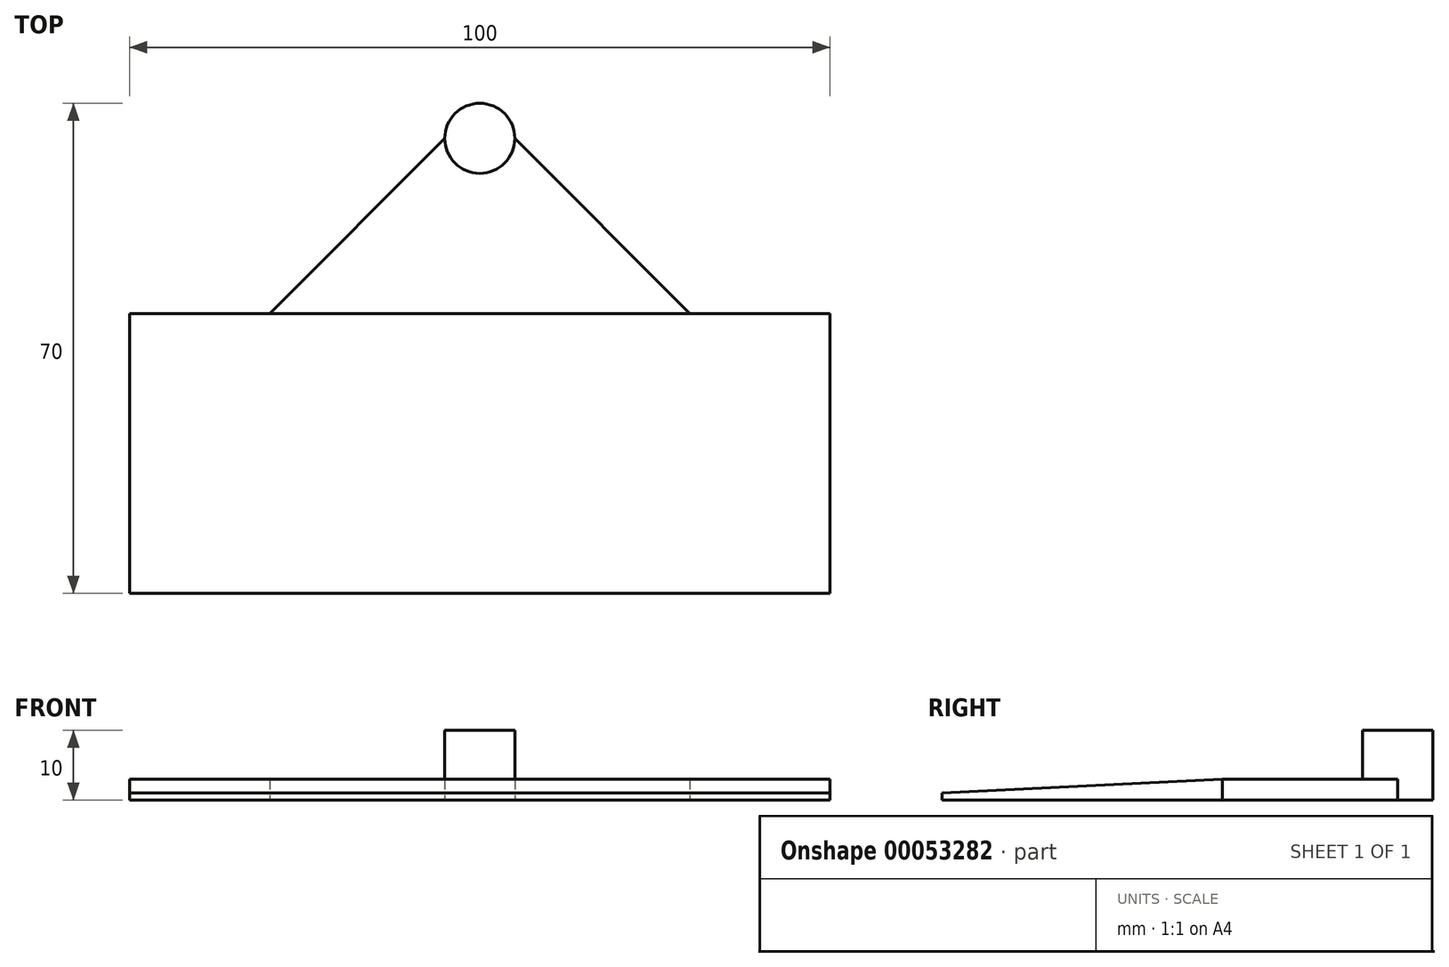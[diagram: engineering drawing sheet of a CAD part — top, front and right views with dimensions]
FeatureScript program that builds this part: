
annotation { "Feature Type Name" : "Feature", "Feature Type Description" : "" }
export const myFeature = defineFeature(function(context is Context, id is Id, definition is map)
    precondition{}
    {
        {
            var Q0;
            Q0=qCreatedBy(makeId("Right.planeOp"),FACE);
            var sketch = newSketch(context, id + "F0", { "sketchPlane" : qUnion([Q0])});
            skLineSegment(sketch, "E0", {"start": v(0, 0) * mm, "end": v(40, 0) * mm});
            skLineSegment(sketch, "E1", {"start": v(40, 0) * mm, "end": v(40, 3) * mm});
            skLineSegment(sketch, "E2", {"start": v(0, 0) * mm, "end": v(0, 1) * mm});
            skLineSegment(sketch, "E3", {"start": v(0, 1) * mm, "end": v(40, 3) * mm});
            skSolve(sketch);
        }
        {
            var Q0;
            Q0=makeQuery(id+"F0.imprint","IMPRINT",FACE,{"disambiguationData":[TD([[makeQuery(id+"F0.imprint","IMPRINT",EDGE,{"derivedFrom":sQuery(id+"F0.wireOp",EDGE,"E0")}),1.0]])]});
            extrude(context, id + "F1", {"entities" : qUnion([Q0]), "depth" : 100 * mm});
        }
        {
            var Q0;
            Q0=makeQuery(id+"F1.opExtrude","SWEPT_FACE",FACE,{"disambiguationData":[OSD([sQuery(id+"F0.wireOp",EDGE,"E0")])]});
            var sketch = newSketch(context, id + "F2", { "sketchPlane" : qUnion([Q0])});
            skLineSegment(sketch, "E4.rect.bottom", {"start": v(55, -65) * mm, "end": v(45, -65) * mm});
            skLineSegment(sketch, "E4.rect.top", {"start": v(55, -15) * mm, "end": v(45, -15) * mm});
            skLineSegment(sketch, "E4.rect.left", {"start": v(55, -65) * mm, "end": v(55, -15) * mm});
            skLineSegment(sketch, "E4.rect.right", {"start": v(45, -65) * mm, "end": v(45, -15) * mm});
            skPoint(sketch, "E4.rect.middle", {"position": v(50, -40) * mm});
            skCircle(sketch, "E5", {"center": v(50, -65) * mm, "radius": 5 * mm});
            skLineSegment(sketch, "E6", {"start": v(55, -65) * mm, "end": v(80, -40) * mm});
            skLineSegment(sketch, "E7", {"start": v(45, -65) * mm, "end": v(20, -40) * mm});
            skSolve(sketch);
        }
        {
            var Q0;
            {var subQ0=sQuery(id+"F2.wireOp",EDGE,"E5");var subQ1=sQuery(id+"F2.wireOp",EDGE,"E4.rect.left");var subQ2=sQuery(id+"F2.wireOp",EDGE,"E4.rect.bottom");var subQ3=makeQuery(id+"F2.imprint","INTERSECT",VERTEX,{"derivedFrom":[subQ2,subQ1,subQ0]});Q0=makeQuery(id+"F2.imprint","IMPRINT",FACE,{"disambiguationData":[TD([[makeQuery(id+"F2.imprint","IMPRINT",EDGE,{"disambiguationData":[TD([[subQ3,-1.0]])],"derivedFrom":subQ1}),1.0]])]});}
            var Q1;
            {var subQ0=sQuery(id+"F2.wireOp",EDGE,"E7");Q1=makeQuery(id+"F2.imprint","IMPRINT",FACE,{"disambiguationData":[TD([[makeQuery(id+"F2.imprint","IMPRINT",EDGE,{"derivedFrom":subQ0}),-1.0]])]});}
            var Q2;
            {var subQ0=sQuery(id+"F2.wireOp",EDGE,"E6");Q2=makeQuery(id+"F2.imprint","IMPRINT",FACE,{"disambiguationData":[TD([[makeQuery(id+"F2.imprint","IMPRINT",EDGE,{"derivedFrom":subQ0}),1.0]])]});}
            extrude(context, id + "F3", {"entities" : qUnion([Q0, Q1, Q2]), "operationType" : NewBodyOperationType.ADD, "oppositeDirection" : true, "depth" : 3 * mm});
        }
        {
            var Q0;
            {var subQ0=sQuery(id+"F2.wireOp",EDGE,"E4.rect.bottom");Q0=makeQuery(id+"F2.imprint","IMPRINT",FACE,{"disambiguationData":[TD([[makeQuery(id+"F2.imprint","IMPRINT",EDGE,{"derivedFrom":subQ0}),-1.0]])]});}
            var Q1;
            {var subQ0=sQuery(id+"F2.wireOp",EDGE,"E4.rect.bottom");Q1=makeQuery(id+"F2.imprint","IMPRINT",FACE,{"disambiguationData":[TD([[makeQuery(id+"F2.imprint","IMPRINT",EDGE,{"derivedFrom":subQ0}),1.0]])]});}
            extrude(context, id + "F4", {"entities" : qUnion([Q0, Q1]), "operationType" : NewBodyOperationType.ADD, "oppositeDirection" : true, "depth" : 10 * mm});
        }
    });
